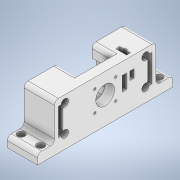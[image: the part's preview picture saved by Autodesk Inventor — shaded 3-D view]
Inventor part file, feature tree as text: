
AUTODESK INVENTOR PART (.ipt)
format: ipt  version: 2020 (Build 240168000, 168)  size: 340,480 bytes
history: native  units: mm
features: extrude x11, sketch x6, projected_geometry x3, other x1, mirror x1
ambient origin geometry x8: Origin, YZ Plane, XZ Plane, XY Plane, X Axis, Y Axis, Z Axis, Center Point
bodies: Body1 (feature_tree)
feature tree (22):
  other  "Bryła1"
  sketch  "Szkic1"
  extrude  "Wyciągnięcie proste1"  Depth=28.0mm
  extrude  "Wyciągnięcie proste2"  Depth=11.0mm
  extrude  "Wyciągnięcie proste12"  Depth=40.0mm
  extrude  "Wyciągnięcie proste4"  Depth=20.0mm
  sketch  "Szkic2"
  extrude  "Wyciągnięcie proste5"  Depth=60.0mm
  extrude  "Wyciągnięcie proste6"  Depth=6.0mm
  mirror  "Odbij1"
  extrude  "Wyciągnięcie proste8"  Depth=3.5mm
  sketch  "Szkic3"
  extrude  "Wyciągnięcie proste7"  TaperAngle=150.0deg  [1 undecoded]
  extrude  "Wyciągnięcie proste9"  TaperAngle=150.0deg  [1 undecoded]
  extrude  "Wyciągnięcie proste10"  Depth=26.0mm
  extrude  "Wyciągnięcie proste11"  Depth=13.0mm
  sketch  "Szkic5"
  projected_geometry  "Pętla rzutowana1"
  sketch  "Szkic6"
  projected_geometry  "Pętla rzutowana2"
  sketch  "Szkic7"
  projected_geometry  "Pętla rzutowana3"
note: 2 required parameter values undecoded (feature->parameter linkage not recoverable at this tier; creation-order binding heuristic only, values carry confidence <= 0.55)
